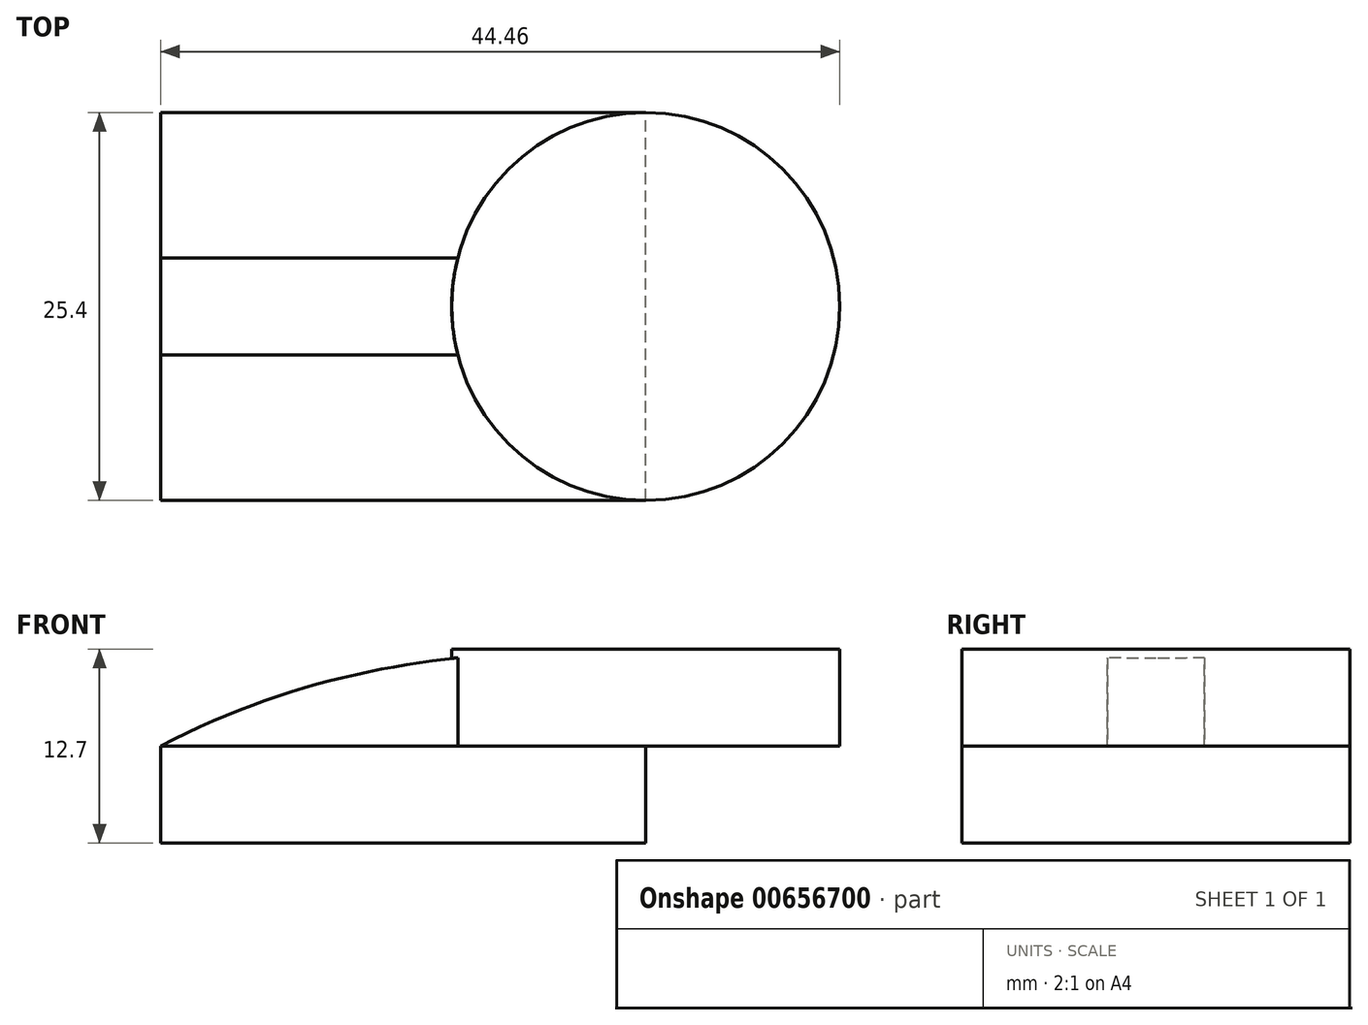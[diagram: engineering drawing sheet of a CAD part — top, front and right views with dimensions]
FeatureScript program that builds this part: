
annotation { "Feature Type Name" : "Feature", "Feature Type Description" : "" }
export const myFeature = defineFeature(function(context is Context, id is Id, definition is map)
    precondition{}
    {
        {
            var Q0;
            Q0=qCreatedBy(makeId("Front.planeOp"),FACE);
            var sketch = newSketch(context, id + "F0", { "sketchPlane" : qUnion([Q0])});
            skLineSegment(sketch, "E0.bottom", {"start": v(15.87, 3.17) * mm, "end": v(-15.88, 3.17) * mm});
            skLineSegment(sketch, "E0.top", {"start": v(15.88, -3.17) * mm, "end": v(-15.88, -3.17) * mm});
            skLineSegment(sketch, "E0.left", {"start": v(15.88, 3.17) * mm, "end": v(15.88, -3.17) * mm});
            skLineSegment(sketch, "E0.right", {"start": v(-15.88, 3.18) * mm, "end": v(-15.88, -3.17) * mm});
            skPoint(sketch, "E0.middle", {"position": v(0, 0) * mm});
            skLineSegment(sketch, "E1.bottom", {"start": v(15.88, 3.17) * mm, "end": v(28.57, 3.17) * mm});
            skLineSegment(sketch, "E1.top", {"start": v(15.88, 9.53) * mm, "end": v(28.57, 9.53) * mm});
            skLineSegment(sketch, "E1.left", {"start": v(15.88, 3.18) * mm, "end": v(15.88, 9.52) * mm});
            skLineSegment(sketch, "E1.right", {"start": v(28.58, 3.18) * mm, "end": v(28.58, 9.52) * mm});
            skFitSpline(sketch, "E2", {"points": [v(-15.88, 3.18) * mm, v(15.88, 9.52) * mm], "startDerivative": vector(32.5, 17.2) * mm, "endDerivative": vector(31.32, 0) * mm});
            skSolve(sketch);
        }
        {
            var Q0;
            Q0=makeQuery(id+"F0.imprint","IMPRINT",FACE,{"disambiguationData":[TD([[makeQuery(id+"F0.imprint","IMPRINT",EDGE,{"derivedFrom":sQuery(id+"F0.wireOp",EDGE,"E0.bottom")}),1.0]])]});
            extrude(context, id + "F1", {"entities" : qUnion([Q0]), "endBound" : BoundingType.SYMMETRIC, "depth" : 25.4 * mm, "offsetDistance" : 25.4 * mm});
        }
        {
            var Q0;
            Q0=makeQuery(id+"F0.imprint","IMPRINT",FACE,{"disambiguationData":[TD([[makeQuery(id+"F0.imprint","IMPRINT",EDGE,{"derivedFrom":sQuery(id+"F0.wireOp",EDGE,"E0.bottom")}),-1.0]])]});
            extrude(context, id + "F2", {"entities" : qUnion([Q0]), "operationType" : NewBodyOperationType.ADD, "endBound" : BoundingType.SYMMETRIC, "depth" : 6.35 * mm, "offsetDistance" : 25.4 * mm});
        }
        {
            var Q0;
            Q0=makeQuery(id+"F0.imprint","IMPRINT",FACE,{"disambiguationData":[TD([[makeQuery(id+"F0.imprint","IMPRINT",EDGE,{"derivedFrom":sQuery(id+"F0.wireOp",EDGE,"E1.bottom")}),1.0]])]});
            var Q1;
            Q1=sQuery(id+"F0.wireOp",EDGE,"E1.left");
            revolve(context, id + "F3", {"operationType" : NewBodyOperationType.ADD, "surfaceOperationType" : NewSurfaceOperationType.NEW, "entities" : qUnion([Q0]), "axis" : qUnion([Q1]), "revolveType" : RevolveType.TWO_DIRECTIONS, "angle" : 90 * degree, "angleBack" : 90 * degree});
        }
    });
